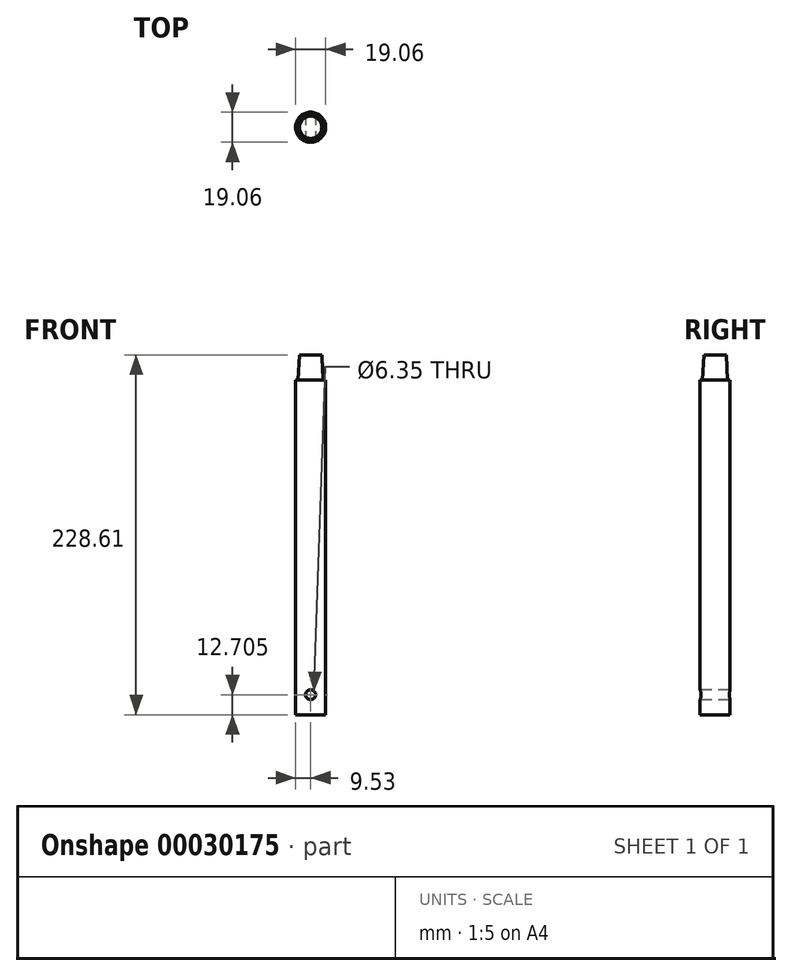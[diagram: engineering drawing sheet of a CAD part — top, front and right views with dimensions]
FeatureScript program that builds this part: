
annotation { "Feature Type Name" : "Feature", "Feature Type Description" : "" }
export const myFeature = defineFeature(function(context is Context, id is Id, definition is map)
    precondition{}
    {
        {
            var Q0;
            Q0=qCreatedBy(makeId("Top.planeOp"),FACE);
            var sketch = newSketch(context, id + "F0", { "sketchPlane" : qUnion([Q0])});
            skCircle(sketch, "E0", {"center": v(0, 0) * mm, "radius": 9.53 * mm});
            skSolve(sketch);
        }
        {
            var Q0;
            Q0 = qSketchRegion(id + "F0", true);
            extrude(context, id + "F1", {"entities" : qUnion([Q0]), "oppositeDirection" : true, "depth" : 212.72 * mm});
        }
        {
            var Q0;
            Q0=makeQuery(id+"F1.opExtrude","CAP_FACE",FACE,{"disambiguationData":[OSD([sQuery(id+"F0.wireOp",EDGE,"E0")])],"isStart":true});
            var sketch = newSketch(context, id + "F2", { "sketchPlane" : qUnion([Q0])});
            skCircle(sketch, "E1", {"center": v(0, 0) * mm, "radius": 7.94 * mm});
            skSolve(sketch);
        }
        {
            var Q0;
            Q0=makeQuery(id+"F2.imprint","IMPRINT",FACE,{"disambiguationData":[TD([[makeQuery(id+"F2.imprint","IMPRINT",EDGE,{"derivedFrom":sQuery(id+"F2.wireOp",EDGE,"E1")}),1.0]])]});
            extrude(context, id + "F3", {"entities" : qUnion([Q0]), "operationType" : NewBodyOperationType.ADD, "depth" : 15.88 * mm, "hasDraft" : true, "draftAngle" : 3 * degree, "draftPullDirection" : true});
        }
        {
            var Q0;
            Q0=qCreatedBy(makeId("Front.planeOp"),FACE);
            var sketch = newSketch(context, id + "F4", { "sketchPlane" : qUnion([Q0])});
            skCircle(sketch, "E2", {"center": v(0, -200.03) * mm, "radius": 3.18 * mm});
            skSolve(sketch);
        }
        {
            var Q0;
            Q0=makeQuery(id+"F4.imprint","IMPRINT",FACE,{"disambiguationData":[TD([[makeQuery(id+"F4.imprint","IMPRINT",EDGE,{"derivedFrom":sQuery(id+"F4.wireOp",EDGE,"E2")}),1.0]])]});
            extrude(context, id + "F5", {"entities" : qUnion([Q0]), "operationType" : NewBodyOperationType.REMOVE, "endBound" : BoundingType.SYMMETRIC, "oppositeDirection" : true, "depth" : 25.4 * mm});
        }
    });
